# Revit family: PRD_AR_WstBns_RODANWasteBin_RODX605SL
name_source: partatom
category: Specialty Equipment
revit_build: Autodesk Revit 2018 (Build: 20190510_1515(x64)
units: mm (PartAtom-declared; Revit-internal decimal feet)

## family parameters
Cut with Voids When Loaded = Yes
Host = Face
OmniClass Number = 23.40.20.31.11
OmniClass Title = Bins
Part Type = Normal
Room Calculation Point = No
Round Connector Dimension = Use Diameter
Shared = No

## types (1)
- RODX605SL
    AssetType = Fixed
    BIMObjectName = PRD_AR_WasteBins_RODANWasteBin_RODX605SL
    BagHolder = Integrated
    Category = Pr_40_50_07_96, Waste bins
    Default Elevation = 400 mm  [stored 1.31234 ft]
    Description = Waste bin for wall mounting or floor standing, made of stainless steel, surface satin finished, material thickness 0.8 mm, self closing lid, folding bag holder, cylinder lock with KWC standard key, approx. 30 liter capacity, includes stainless steel screws and dowels.
    DurationUnit = year
    Features = stainless steel, surface satin finished
    FillingVolume = 30.00 liter
    Finish = satin finished
    GrossWeight = 5.78 kg
    IfcExportAs = IfcFurnitureType
    IfcExportType = USERDEFINED
    IntegralAccessories = incl. stainless steel screws and dowels
    IsBuiltIn = TRUE
    Lid = Yes
    Lock = Key-lock
    MainColor = stainless steel
    Manufacturer = KWC Group AG
    ManufacturerName = KWC Group AG
    ManufacturerURL = www.kwc.com
    Material = stainless steel
    MaterialCode = 1.4301
    MaterialThickness = 0.80 mm
    Model = RODX605SL
    ModelNumber = 2000103806
    ModelReference = RODX605SL
    NBSDescription = Waste bins
    NBSReference = 45-35-72/380
    Name = Waste Bin RODX605SL
    NetWeight = 5.00 kg
    NominalDepth = 210 mm  [stored 0.688976 ft]
    NominalHeight = 610 mm  [stored 2.00131 ft]
    NominalWidth = 275 mm  [stored 0.902231 ft]
    ProductInformation = https://pim.kwc.com
    Size = 275 x 610 x 210 mm
    Style = waste bin
    TypeOfFixing = Screw
    TypeOfMounting = Various types
    URL = www.kwc.com
    Uniclass2015Code = Pr_40_50_07_96
    Uniclass2015Title = Waste bins
    Uniclass2015Version = Products v1.10
    Version = 1
    WarrantyDurationUnit = year
    WasteBinMaterial = PRD_AR_StainlessSteel_SatinFinished

note: [stored X ft] marks values corroborated as IEEE doubles in the binary element streams (Revit-internal decimal feet)

## geometry (parser evidence)
native form markers: Sweep x4
no freeform markers — native parametric forms only
